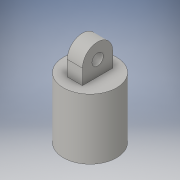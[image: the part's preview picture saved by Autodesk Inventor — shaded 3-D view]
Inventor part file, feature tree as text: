
AUTODESK INVENTOR PART (.ipt)
format: ipt  version: 2016 (Build 200138000, 138)  size: 139,776 bytes
history: native  units: in
note: dims shown in document units (in); Inventor stores cm internally (conversion verified against a paired STEP export)
features: sketch x6, extrude x5, revolve x1, fillet x1
ambient origin geometry x8: Origin, YZ Plane, XZ Plane, XY Plane, X Axis, Y Axis, Z Axis, Center Point
bodies: Solid1 (feature_tree)
feature tree (13):
  revolve  "Revolution1"  [1 undecoded]
  extrude  "Extrusion1"  Depth=0.25in TaperAngle=0.0deg
  extrude  "Extrusion2"  Depth=2.0in
  extrude  "Extrusion3"  Depth=1.0in
  extrude  "Extrusion6"  Depth=2.0in TaperAngle=0.0deg
  fillet  "Fillet2"  [1 undecoded]
  extrude  "Extrusion7"  [1 undecoded]
  sketch  "Sketch1"  dims[d2=180.0deg d3=0.25in d4=0.0in]
  sketch  "Sketch2"  dims[d5=0.25in d6=0.0in d7=0.5in d8=0.0in]
  sketch  "Sketch3"  dims[d9=2.0in d10=2.0in]
  sketch  "Sketch4"  dims[d17=2.0in d18=0.0in d19=1.0in]
  sketch  "Sketch5"  dims[d20=0.75in d21=2.0in d22=0.0in]
  sketch  "Sketch7"
note: 3 required parameter values undecoded (feature->parameter linkage not recoverable at this tier; creation-order binding heuristic only, values carry confidence <= 0.55)